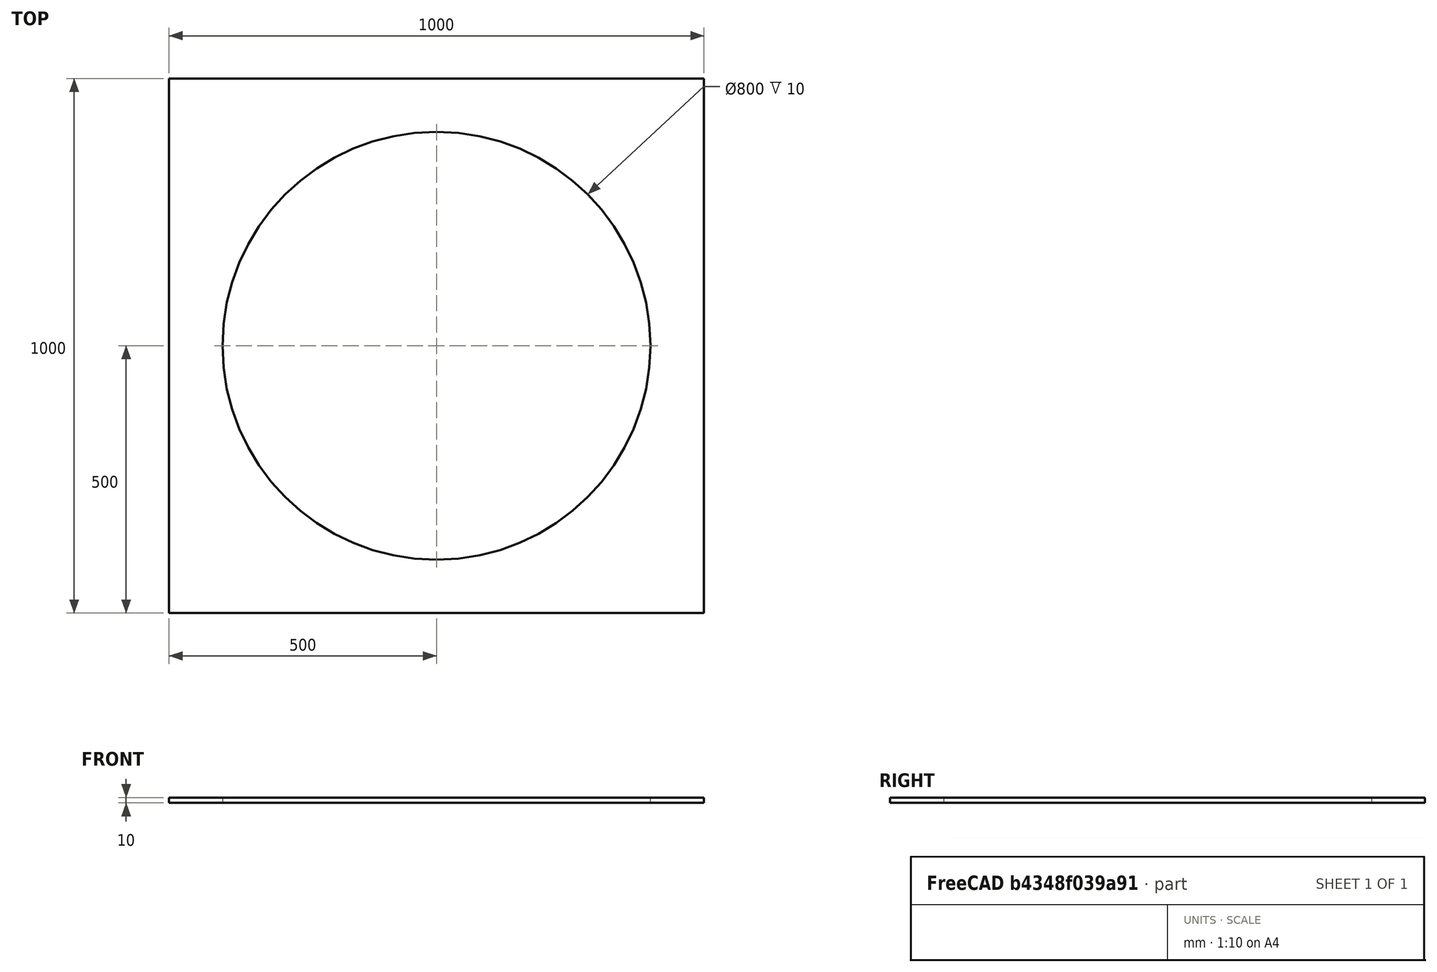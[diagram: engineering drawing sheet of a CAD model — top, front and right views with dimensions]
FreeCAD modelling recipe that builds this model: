
FCSTD DOCUMENT  (FreeCAD 0.21R33694 (Git))
Label: shear_panel_with_hole
License: All rights reserved
LicenseURL: http://en.wikipedia.org/wiki/All_rights_reserved
objects: Fem::ConstraintForce×4, Fem::ConstraintDisplacement×2, Part::Box×1, App::MaterialObjectPython×1, Fem::FemSolverObjectPython×1, Fem::ConstraintFixed×1, Part::Cylinder×1, Part::Cut×1, Fem::FemMeshObjectPython×1, Fem::FemAnalysis×1
note: 3 computed .brp shape members not serialized (recipe doc carries the construction recipe); baked Part::Feature solids carry a one-line shape summary decoded from their .brp

FEATURE [Part::Box] Box  label="Cube"
  AttacherType = Attacher::AttachEngine3D
  Height = 10
  Length = 1000
  Width = 1000
FEATURE [Fem::ConstraintDisplacement] ConstraintDisplacement
  NormalDirection = (0,0,1)
  Normals = (16) [(0,0,1),(0,0,1),(0,0,1),(0,0,1),(0,0,1),(0,0,1),(0,0,1),(0,0,1),(0,0,1),(0,0,1),(0,0,1),(0,0,1),(0,0,1),(0,0,1),(0,0,1),(0,0,1)]
  Points = (16) [(0,0,0),(333.333,0,0),(666.667,0,0),(1000,0,0),(0,0,0),(0,333.333,0),(0,666.667,0),(0,1000,0),(1000,0,0),(1000,333.333,0),(1000,666.667,0),+5 more]
  References = -> [Box]
  Scale = 33
  hasXFormula = false
  hasYFormula = false
  hasZFormula = false
  rotxFix = false
  rotxFree = true
  rotyFix = false
  rotyFree = true
  rotzFix = false
  rotzFree = true
  useFlowSurfaceForce = false
  xDisplacement = 0
  xFix = false
  xFree = true
  xRotation = 0
  yDisplacement = 0
  yFix = false
  yFree = true
  yRotation = 0
  zDisplacement = 0
  zFix = false
  zFree = false
  zRotation = 0
FEATURE [Fem::ConstraintForce] ConstraintForce
  Direction = -> Box [Edge12]
  DirectionVector = (1,0,0)
  Force = 1000000
  NormalDirection = (0,1,0)
  Points = (15) [(0,1000,0),(0,1000,5),(0,1000,10),(250,1000,0),(250,1000,5),(250,1000,10),(500,1000,0),(500,1000,5),(500,1000,10),(750,1000,0),(750,1000,5),+4 more]
  References = -> [Box]
FEATURE [Fem::ConstraintForce] ConstraintForce001
  Direction = -> Box [Edge10]
  DirectionVector = (-1,0,0)
  Force = 1000000
  NormalDirection = (0,-1,0)
  Points = (15) [(0,0,0),(0,0,5),(0,0,10),(250,0,0),(250,0,5),(250,0,10),(500,0,0),(500,0,5),(500,0,10),(750,0,0),(750,0,5),(750,0,10),(1000,0,0),(1000,0,5),+1 more]
  References = -> [Box]
  Reversed = true
FEATURE [Fem::ConstraintForce] ConstraintForce002
  Direction = -> Box [Edge6]
  DirectionVector = (0,1,0)
  Force = 1000000
  NormalDirection = (1,0,0)
  Points = (15) [(1000,1000,0),(1000,1000,5),(1000,1000,10),(1000,750,0),(1000,750,5),(1000,750,10),(1000,500,0),(1000,500,5),(1000,500,10),(1000,250,0),(1000,250,5),+4 more]
  References = -> [Box]
FEATURE [Fem::ConstraintForce] ConstraintForce003
  Direction = -> Box [Edge2]
  DirectionVector = (0,-1,0)
  Force = 1000000
  NormalDirection = (-1,0,0)
  Points = (15) [(0,1000,0),(0,1000,5),(0,1000,10),(0,750,0),(0,750,5),(0,750,10),(0,500,0),(0,500,5),(0,500,10),(0,250,0),(0,250,5),(0,250,10),(0,0,0),(0,0,5),+1 more]
  References = -> [Box]
  Reversed = true
FEATURE [App::MaterialObjectPython] MaterialSolid  # material (typed FeaturePython)
  Category = 0
  Material = AuthorAndLicense=(c) 2014 M. Münch - GNU Lesser General Public License (LGPL),CardName=Steel-St-E-315,Density=7800 kg/m^3,Father=Metal,+13 more (map truncated)
FEATURE [Fem::FemSolverObjectPython] SolverCcxTools  # FEM object (typed FeaturePython)
  AnalysisType = 0
  BeamShellResultOutput3D = false
  BucklingFactors = 1
  EigenmodeHighLimit = 1000000
  EigenmodeLowLimit = 0
  EigenmodesCount = 10
  GeometricalNonlinearity = 0
  IterationsControlParameterCutb = 0.25,0.5,0.75,0.85,,,1.5,
  IterationsControlParameterIter = 4,8,9,200,10,400,,200,,
  IterationsControlParameterTimeUse = false
  IterationsThermoMechMaximum = 2000
  IterationsUserDefinedIncrementations = false
  IterationsUserDefinedTimeStepLength = false
  MaterialNonlinearity = 0
  MatrixSolverType = 0
  SplitInputWriter = false
  ThermoMechSteadyState = true
  TimeEnd = 1
  TimeInitialStep = 0.01
FEATURE [Fem::ConstraintFixed] ConstraintFixed
  NormalDirection = (0,0,1)
  Normals = (2) [(0,0,1),(0,0,1)]
  Points = (2) [(1000,1000,0),(1000,1000,10)]
  References = -> [Box]
FEATURE [Fem::ConstraintDisplacement] ConstraintDisplacement001
  NormalDirection = (0,0,1)
  Normals = (2) [(0,0,1),(0,0,1)]
  Points = (2) [(1000,0,0),(1000,0,10)]
  References = -> [Box]
  hasXFormula = false
  hasYFormula = false
  hasZFormula = false
  rotxFix = false
  rotxFree = true
  rotyFix = false
  rotyFree = true
  rotzFix = false
  rotzFree = true
  useFlowSurfaceForce = false
  xDisplacement = 0
  xFix = false
  xFree = false
  xRotation = 0
  yDisplacement = 0
  yFix = false
  yFree = true
  yRotation = 0
  zDisplacement = 0
  zFix = false
  zFree = true
  zRotation = 0
FEATURE [Part::Cylinder] Cylinder
  Angle = 360
  AttacherType = Attacher::AttachEngine3D
  FirstAngle = 0
  Height = 10
  Placement = pos=(500,500,0) rot=(0,0,1;0rad)
  Radius = 400
  SecondAngle = 0
FEATURE [Part::Cut] Cut
  Base = -> Box
  Tool = -> Cylinder
FEATURE [Fem::FemMeshObjectPython] FEMMeshGmsh  # FEM object (typed FeaturePython)
  Algorithm2D = 0
  Algorithm3D = 0
  CharacteristicLengthMax = 50
  CharacteristicLengthMin = 0
  CoherenceMesh = true
  ElementDimension = 0
  ElementOrder = 1
  GeometryTolerance = 1e-06
  GroupsOfNodes = false
  HighOrderOptimize = 0
  MeshSizeFromCurvature = 12
  OptimizeNetgen = false
  OptimizeStd = true
  Part = -> Cut
  RecombinationAlgorithm = 0
  Recombine3DAll = false
  RecombineAll = false
  SecondOrderLinear = false
FEATURE [Fem::FemAnalysis] Analysis
  Group = -> [ConstraintDisplacement,ConstraintForce,ConstraintForce001,ConstraintForce002,ConstraintForce003,MaterialSolid,SolverCcxTools,ConstraintFixed,ConstraintDisplacement001,FEMMeshGmsh]
